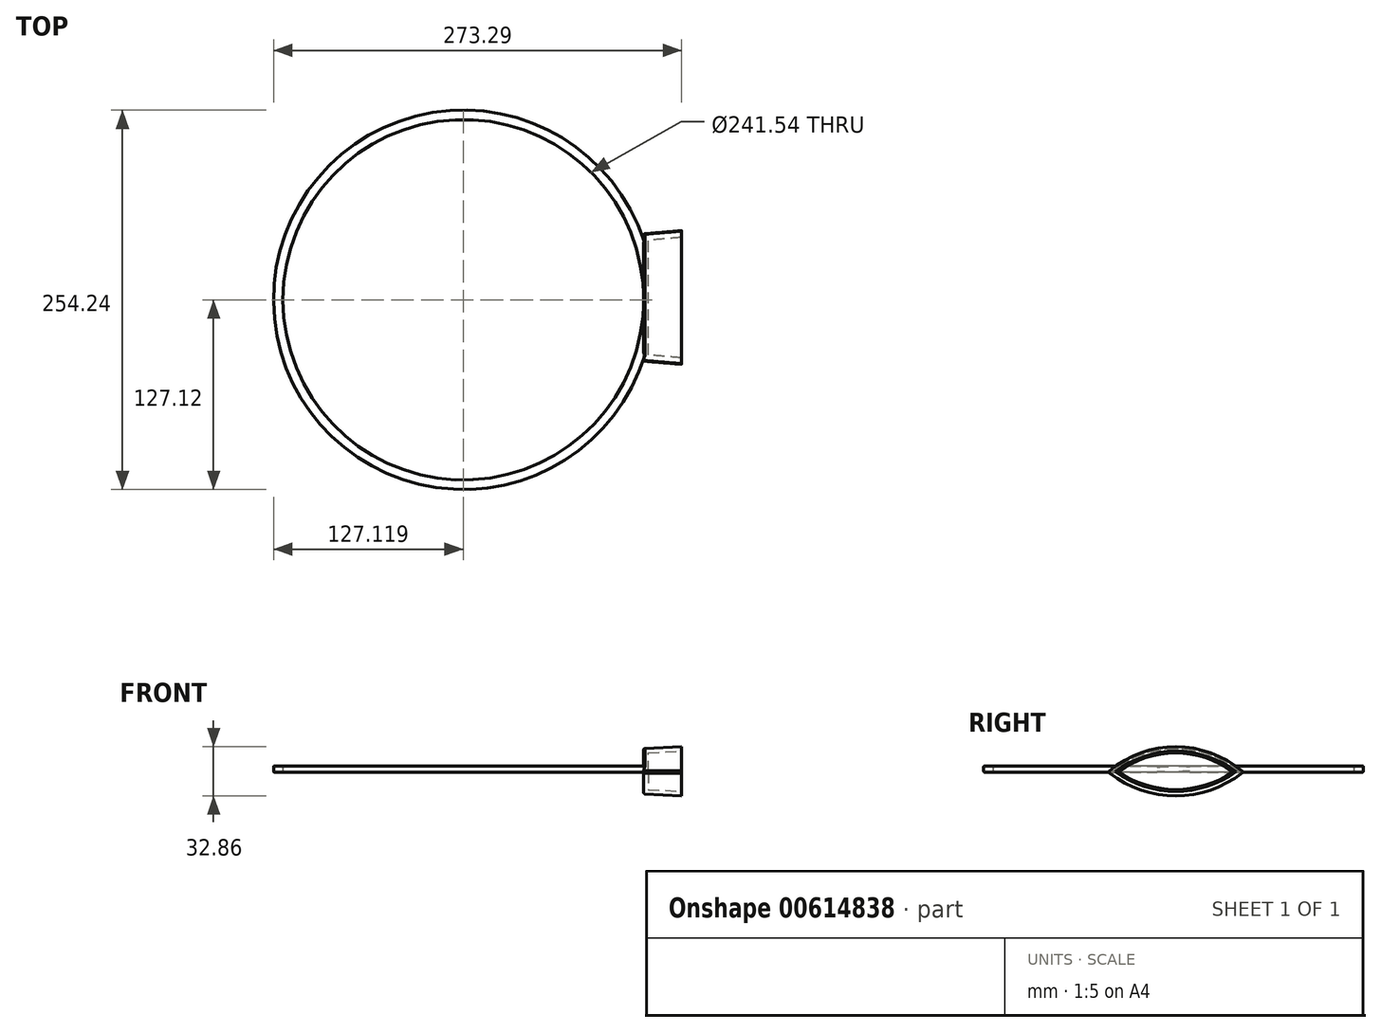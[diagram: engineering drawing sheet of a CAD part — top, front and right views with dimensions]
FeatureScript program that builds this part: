
annotation { "Feature Type Name" : "Feature", "Feature Type Description" : "" }
export const myFeature = defineFeature(function(context is Context, id is Id, definition is map)
    precondition{}
    {
        {
            var Q0;
            Q0=qCreatedBy(makeId("Right.planeOp"),FACE);
            var sketch = newSketch(context, id + "F0", { "sketchPlane" : qUnion([Q0])});
            skArc(sketch, "E0", {"start": v(44.54, 0) * mm, "mid": v(1.42, 15.63) * mm, "end": v(-41.7, 0) * mm});
            skArc(sketch, "E1", {"start": v(-41.7, 0) * mm, "mid": v(1.42, -14.57) * mm, "end": v(44.54, 0) * mm});
            skSolve(sketch);
        }
        {
            var Q0;
            Q0=makeQuery(id+"F0.imprint","IMPRINT",FACE,{"disambiguationData":[TD([[makeQuery(id+"F0.imprint","IMPRINT",EDGE,{"derivedFrom":sQuery(id+"F0.wireOp",EDGE,"E0")}),1.0]])]});
            extrude(context, id + "F1", {"entities" : qUnion([Q0]), "depth" : 25.4 * mm, "offsetDistance" : 25.4 * mm, "hasDraft" : true, "draftAngle" : 3 * degree});
        }
        {
            var Q0;
            Q0=makeQuery(id+"F1.opExtrude","CAP_FACE",FACE,{"disambiguationData":[OSD([sQuery(id+"F0.wireOp",EDGE,"E0"),sQuery(id+"F0.wireOp",EDGE,"E1")])],"isStart":false});
            shell(context, id + "F2", {"entities" : qUnion([Q0]), "thickness" : 3 * mm});
        }
        {
            var Q0;
            Q0=qCreatedBy(makeId("Top.planeOp"),FACE);
            var sketch = newSketch(context, id + "F3", { "sketchPlane" : qUnion([Q0])});
            skCircle(sketch, "E2", {"center": v(-120.77, 0) * mm, "radius": 120.77 * mm});
            skCircle(sketch, "E3.0", {"center": v(-120.77, 0) * mm, "radius": 127.12 * mm});
            skSolve(sketch);
        }
        {
            var Q0;
            Q0 = qSketchRegion(id + "F3", true);
            extrude(context, id + "F4", {"entities" : qUnion([Q0]), "operationType" : NewBodyOperationType.ADD, "depth" : 4 * mm, "offsetDistance" : 25.4 * mm});
        }
        {
            var Q0;
            {var subQ0=sQuery(id+"F3.wireOp",EDGE,"E3.0");Q0=makeQuery(id+"F4.boolean.opBoolean","SPLIT",EDGE,{"disambiguationData":[TD([makeQuery(id+"F1.opExtrude","CAP_FACE",FACE,{"disambiguationData":[OSD([sQuery(id+"F0.wireOp",EDGE,"E0"),sQuery(id+"F0.wireOp",EDGE,"E1")])],"isStart":true})])],"derivedFrom":makeQuery(id+"F4.opExtrude","CAP_EDGE",EDGE,{"disambiguationData":[OSD([subQ0])],"isStart":true})});}
            var Q1;
            {var subQ0=sQuery(id+"F3.wireOp",EDGE,"E3.0");Q1=makeQuery(id+"F4.boolean.opBoolean","SPLIT",EDGE,{"disambiguationData":[TD([makeQuery(id+"F1.opExtrude","SWEPT_FACE",FACE,{"disambiguationData":[OSD([sQuery(id+"F0.wireOp",EDGE,"E0")])]})])],"derivedFrom":makeQuery(id+"F4.opExtrude","CAP_EDGE",EDGE,{"disambiguationData":[OSD([subQ0])],"isStart":false})});}
            var Q2;
            Q2=makeQuery(id+"F4.opExtrude","CAP_EDGE",EDGE,{"disambiguationData":[OSD([sQuery(id+"F3.wireOp",EDGE,"E2")])],"isStart":true});
            fillet(context, id + "F5", {"entities" : qUnion([Q0, Q1, Q2]), "radius" : 0.5 * mm, "tangentPropagation" : true, "allowEdgeOverflow" : false});
        }
        {
            var Q0;
            Q0=makeQuery(id+"F4.opExtrude","CAP_EDGE",EDGE,{"disambiguationData":[OSD([sQuery(id+"F3.wireOp",EDGE,"E2")])],"isStart":false});
            fillet(context, id + "F6", {"entities" : qUnion([Q0]), "radius" : 0.5 * mm, "tangentPropagation" : true, "allowEdgeOverflow" : false});
        }
        {
            var Q0;
            {var subQ0=sQuery(id+"F0.wireOp",EDGE,"E0");var subQ1=makeQuery(id+"F1.opExtrude","SWEPT_FACE",FACE,{"disambiguationData":[OSD([subQ0])]});var subQ2=sQuery(id+"F0.wireOp",EDGE,"E1");var subQ3=makeQuery(id+"F1.opExtrude","CAP_FACE",FACE,{"disambiguationData":[OSD([subQ0,subQ2])],"isStart":true});var subQ4=sQuery(id+"F3.wireOp",EDGE,"E3.0");var subQ5=makeQuery(id+"F1.opExtrude","CAP_EDGE",EDGE,{"disambiguationData":[OSD([subQ0])],"isStart":true});Q0=makeQuery(id+"F5.opFillet","MERGE",EDGE,{"derivedFrom":[makeQuery(id+"F4.boolean.opBoolean","SPLIT",EDGE,{"disambiguationData":[TD([subQ1,subQ3,makeQuery(id+"F1.opExtrude","SWEPT_FACE",FACE,{"disambiguationData":[OSD([subQ2])]}),makeQuery(id+"F4.opExtrude","SWEPT_FACE",FACE,{"disambiguationData":[OSD([subQ4])]})]),OD(0.0)],"derivedFrom":subQ5}),makeQuery(id+"F4.boolean.opBoolean","SPLIT",EDGE,{"disambiguationData":[TD([subQ1,subQ3,makeQuery(id+"F4.opExtrude","CAP_FACE",FACE,{"disambiguationData":[OSD([sQuery(id+"F3.wireOp",EDGE,"E2"),subQ4])],"isStart":false})])],"derivedFrom":subQ5})]});}
            fillet(context, id + "F7", {"entities" : qUnion([Q0]), "radius" : 0.7 * mm, "tangentPropagation" : true, "allowEdgeOverflow" : false});
        }
        {
            var Q0;
            Q0=makeQuery(id+"F1.opExtrude","CAP_EDGE",EDGE,{"disambiguationData":[OSD([sQuery(id+"F0.wireOp",EDGE,"E1")])],"isStart":true});
            fillet(context, id + "F8", {"entities" : qUnion([Q0]), "radius" : 0.7 * mm, "tangentPropagation" : true, "allowEdgeOverflow" : false});
        }
        {
            var Q0;
            {var subQ0=sQuery(id+"F0.wireOp",EDGE,"E1");var subQ1=sQuery(id+"F0.wireOp",EDGE,"E0");Q0=makeQuery(id+"F1.opExtrude","SWEPT_EDGE",EDGE,{"disambiguationData":[OSD([subQ1,subQ0]),TDD([makeQuery(id+"F0.imprint","INTERSECT",VERTEX,{"disambiguationData":[OD(1.0)],"derivedFrom":[subQ1,subQ0]})])]});}
            fillet(context, id + "F9", {"entities" : qUnion([Q0]), "radius" : 1 * mm, "tangentPropagation" : true, "allowEdgeOverflow" : false});
        }
        {
            var Q0;
            {var subQ0=sQuery(id+"F3.wireOp",EDGE,"E3.0");Q0=makeQuery(id+"F4.boolean.opBoolean","SPLIT",FACE,{"disambiguationData":[TD([makeQuery(id+"F2.opShell","OFFSET_FACE",FACE,{"disambiguationData":[OSD([sQuery(id+"F0.wireOp",EDGE,"E0"),sQuery(id+"F0.wireOp",EDGE,"E1")])]})])],"derivedFrom":makeQuery(id+"F4.opExtrude","CAP_FACE",FACE,{"disambiguationData":[OSD([sQuery(id+"F3.wireOp",EDGE,"E2"),subQ0])],"isStart":true})});}
            extrude(context, id + "F10", {"entities" : qUnion([Q0]), "operationType" : NewBodyOperationType.REMOVE, "oppositeDirection" : true, "depth" : 4 * mm, "offsetDistance" : 25.4 * mm});
        }
    });
